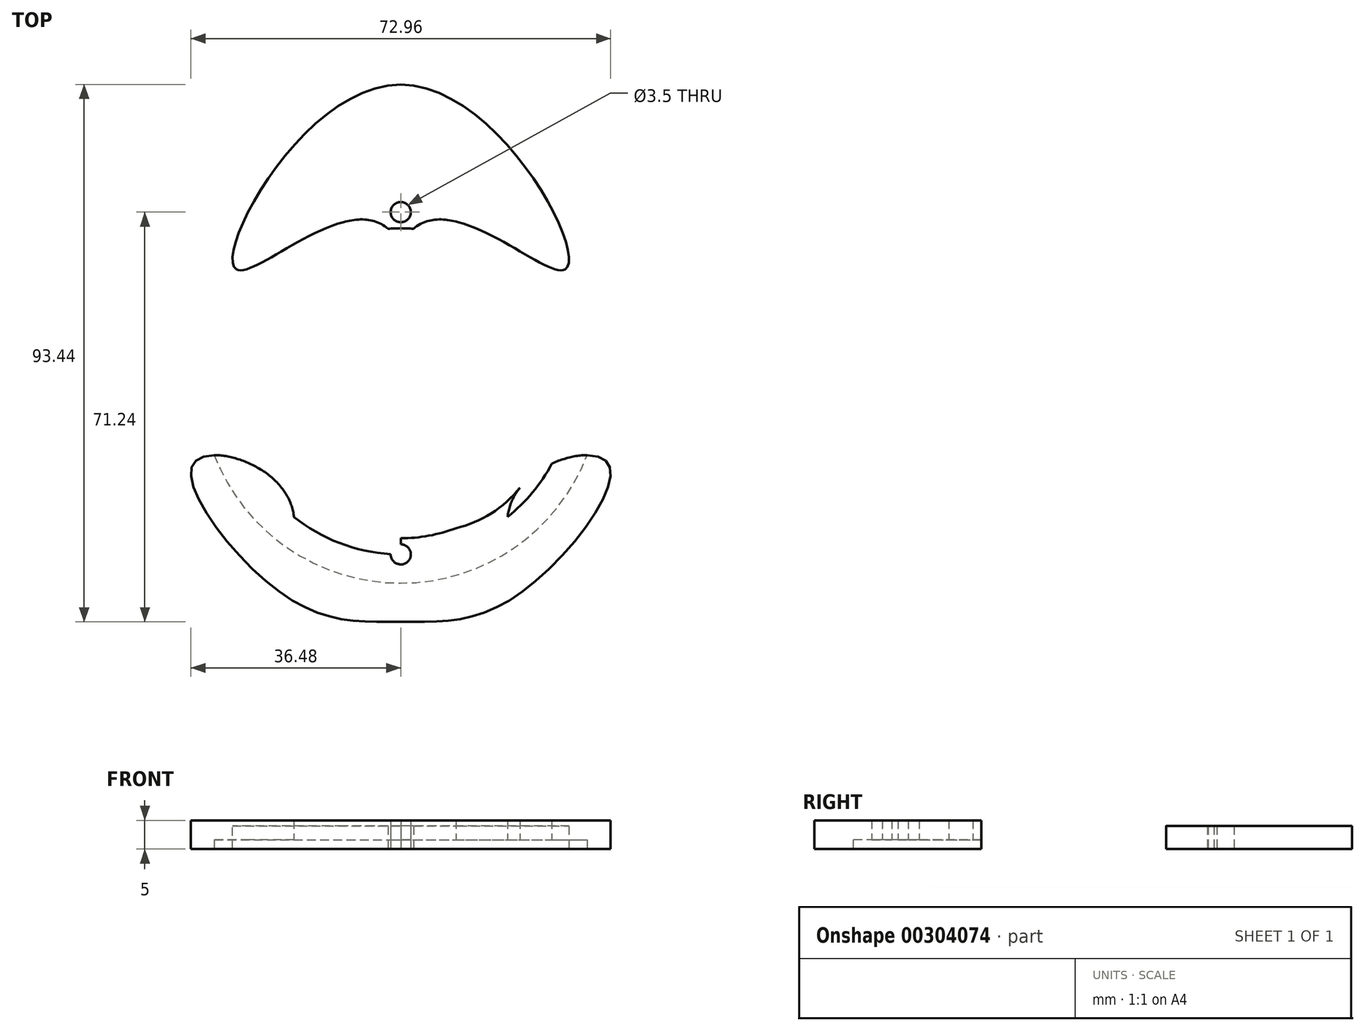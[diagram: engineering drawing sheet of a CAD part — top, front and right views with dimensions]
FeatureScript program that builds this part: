
annotation { "Feature Type Name" : "Feature", "Feature Type Description" : "" }
export const myFeature = defineFeature(function(context is Context, id is Id, definition is map)
    precondition{}
    {
        {
            var Q0;
            Q0=qCreatedBy(makeId("Top.planeOp"),FACE);
            var sketch = newSketch(context, id + "F0", { "sketchPlane" : qUnion([Q0])});
            skCircle(sketch, "E0", {"center": v(0, 0) * mm, "radius": 29.75 * mm});
            skCircle(sketch, "E1.0", {"center": v(0, 0) * mm, "radius": 34.75 * mm});
            skCircle(sketch, "E2.0", {"center": v(0, 0) * mm, "radius": 26.95 * mm});
            skCircle(sketch, "E3", {"center": v(0, 29.75) * mm, "radius": 1.75 * mm});
            skLineSegment(sketch, "E4", {"start": v(0, 39.55) * mm, "end": v(0, 26.95) * mm});
            skCircle(sketch, "E5", {"center": v(0, -29.75) * mm, "radius": 1.75 * mm});
            skLineSegment(sketch, "E6", {"start": v(0, -26.95) * mm, "end": v(1.75, -26.9) * mm});
            skLineSegment(sketch, "E7", {"start": v(1.75, -26.9) * mm, "end": v(9.3, -25.25) * mm});
            skFitSpline(sketch, "E8", {"points": [v(18.58, -23.24) * mm, v(35.7, -13.5) * mm, v(20.62, -36.6) * mm, v(0, -41.48) * mm], "startDerivative": vector(8.66, 84.64) * mm, "endDerivative": vector(-64.45, 0.22) * mm});
            skArc(sketch, "E9.filletArc", {"start": v(9.3, -25.25) * mm, "mid": v(15.63, -22.69) * mm, "end": v(20.72, -18.15) * mm});
            skLineSegment(sketch, "E10", {"start": v(0, -26.95) * mm, "end": v(0, -41.48) * mm});
            skFitSpline(sketch, "E11.MirrorCS", {"points": [v(-18.58, -23.24) * mm, v(-35.7, -13.5) * mm, v(-20.62, -36.6) * mm, v(0, -41.48) * mm], "startDerivative": vector(-8.66, 84.64) * mm, "endDerivative": vector(64.45, 0.22) * mm});
            skLineSegment(sketch, "E12.MirrorCS", {"start": v(0, -26.95) * mm, "end": v(-1.75, -26.9) * mm});
            skLineSegment(sketch, "E13.MirrorCS", {"start": v(-1.75, -26.9) * mm, "end": v(-9.3, -25.25) * mm});
            skArc(sketch, "E14.MirrorCS", {"start": v(-9.3, -25.25) * mm, "mid": v(-15.63, -22.69) * mm, "end": v(-20.72, -18.15) * mm});
            skLineSegment(sketch, "E15", {"start": v(0, 26.95) * mm, "end": v(-2.22, 26.86) * mm});
            skLineSegment(sketch, "E16", {"start": v(-2.22, 26.86) * mm, "end": v(-2.22, 26.86) * mm});
            skFitSpline(sketch, "E17", {"points": [v(-2.22, 26.86) * mm, v(-28.57, 19.79) * mm, v(0, 51.95) * mm], "startDerivative": vector(-50.1, 44.21) * mm, "endDerivative": vector(93.8, 1.88) * mm});
            skLineSegment(sketch, "E18", {"start": v(0, 51.95) * mm, "end": v(0, 39.55) * mm});
            skFitSpline(sketch, "E19.MirrorCS", {"points": [v(2.22, 26.86) * mm, v(28.57, 19.79) * mm, v(0, 51.95) * mm], "startDerivative": vector(50.1, 44.21) * mm, "endDerivative": vector(-93.8, 1.88) * mm});
            skSolve(sketch);
        }
        {
            var Q0;
            {var subQ3=sQuery(id+"F0.wireOp",EDGE,"E0");var subQ5=sQuery(id+"F0.wireOp",EDGE,"E5");var subQ6=makeQuery(id+"F0.imprint","INTERSECT",VERTEX,{"disambiguationData":[OD(1.0)],"derivedFrom":[subQ3,subQ5]});Q0=makeQuery(id+"F0.imprint","IMPRINT",FACE,{"disambiguationData":[TD([[makeQuery(id+"F0.imprint","IMPRINT",EDGE,{"disambiguationData":[TD([[subQ6,-1.0]])],"derivedFrom":subQ3}),-1.0]])]});}
            var Q1;
            {var subQ0=sQuery(id+"F0.wireOp",EDGE,"E8");var subQ1=sQuery(id+"F0.wireOp",EDGE,"E1.0");var subQ2=makeQuery(id+"F0.imprint","INTERSECT",VERTEX,{"derivedFrom":[subQ1,subQ0]});Q1=makeQuery(id+"F0.imprint","IMPRINT",FACE,{"disambiguationData":[TD([[makeQuery(id+"F0.imprint","IMPRINT",EDGE,{"disambiguationData":[TD([[subQ2,1.0]])],"derivedFrom":subQ1}),-1.0]])]});}
            var Q2;
            {var subQ7=sQuery(id+"F0.wireOp",EDGE,"E5");var subQ8=sQuery(id+"F0.wireOp",EDGE,"E0");var subQ9=makeQuery(id+"F0.imprint","INTERSECT",VERTEX,{"disambiguationData":[OD(1.0)],"derivedFrom":[subQ8,subQ7]});Q2=makeQuery(id+"F0.imprint","IMPRINT",FACE,{"disambiguationData":[TD([[makeQuery(id+"F0.imprint","IMPRINT",EDGE,{"disambiguationData":[TD([[subQ9,-1.0]])],"derivedFrom":subQ8}),1.0]])]});}
            var Q3;
            {var subQ0=sQuery(id+"F0.wireOp",EDGE,"E11.MirrorCS");var subQ1=sQuery(id+"F0.wireOp",EDGE,"E1.0");var subQ2=makeQuery(id+"F0.imprint","INTERSECT",VERTEX,{"derivedFrom":[subQ1,subQ0]});Q3=makeQuery(id+"F0.imprint","IMPRINT",FACE,{"disambiguationData":[TD([[makeQuery(id+"F0.imprint","IMPRINT",EDGE,{"disambiguationData":[TD([[subQ2,-1.0]])],"derivedFrom":subQ1}),-1.0]])]});}
            var Q4;
            {var subQ5=sQuery(id+"F0.wireOp",EDGE,"E11.MirrorCS");var subQ7=sQuery(id+"F0.wireOp",EDGE,"E0");var subQ9=makeQuery(id+"F0.imprint","INTERSECT",VERTEX,{"derivedFrom":[subQ7,subQ5]});Q4=makeQuery(id+"F0.imprint","IMPRINT",FACE,{"disambiguationData":[TD([[makeQuery(id+"F0.imprint","IMPRINT",EDGE,{"disambiguationData":[TD([[subQ9,-1.0]])],"derivedFrom":subQ7}),-1.0]])]});}
            var Q5;
            {var subQ1=sQuery(id+"F0.wireOp",EDGE,"E0");var subQ11=sQuery(id+"F0.wireOp",EDGE,"E11.MirrorCS");var subQ12=makeQuery(id+"F0.imprint","INTERSECT",VERTEX,{"derivedFrom":[subQ1,subQ11]});Q5=makeQuery(id+"F0.imprint","IMPRINT",FACE,{"disambiguationData":[TD([[makeQuery(id+"F0.imprint","IMPRINT",EDGE,{"disambiguationData":[TD([[subQ12,-1.0]])],"derivedFrom":subQ1}),1.0]])]});}
            extrude(context, id + "F1", {"entities" : qUnion([Q0, Q1, Q2, Q3, Q4, Q5]), "depth" : 5 * mm});
        }
        {
            var Q0;
            {var subQ0=sQuery(id+"F0.wireOp",EDGE,"0fa87bf3-afe1-459e-863f-c668f79fc1950.MirrorCS");var subQ1=sQuery(id+"F0.wireOp",EDGE,"E0");var subQ2=makeQuery(id+"F0.imprint","INTERSECT",VERTEX,{"derivedFrom":[subQ1,subQ0]});Q0=makeQuery(id+"F0.imprint","IMPRINT",FACE,{"disambiguationData":[TD([[makeQuery(id+"F0.imprint","IMPRINT",EDGE,{"disambiguationData":[TD([[subQ2,-1.0]])],"derivedFrom":subQ1}),-1.0]])]});}
            var Q1;
            {var subQ5=sQuery(id+"F0.wireOp",EDGE,"E11.MirrorCS");var subQ7=sQuery(id+"F0.wireOp",EDGE,"E0");var subQ9=makeQuery(id+"F0.imprint","INTERSECT",VERTEX,{"derivedFrom":[subQ7,subQ5]});Q1=makeQuery(id+"F0.imprint","IMPRINT",FACE,{"disambiguationData":[TD([[makeQuery(id+"F0.imprint","IMPRINT",EDGE,{"disambiguationData":[TD([[subQ9,-1.0]])],"derivedFrom":subQ7}),-1.0]])]});}
            var Q2;
            {var subQ3=sQuery(id+"F0.wireOp",EDGE,"E0");var subQ5=sQuery(id+"F0.wireOp",EDGE,"E5");var subQ6=makeQuery(id+"F0.imprint","INTERSECT",VERTEX,{"disambiguationData":[OD(1.0)],"derivedFrom":[subQ3,subQ5]});Q2=makeQuery(id+"F0.imprint","IMPRINT",FACE,{"disambiguationData":[TD([[makeQuery(id+"F0.imprint","IMPRINT",EDGE,{"disambiguationData":[TD([[subQ6,-1.0]])],"derivedFrom":subQ3}),-1.0]])]});}
            var Q3;
            {var subQ0=sQuery(id+"F0.wireOp",EDGE,"E10");var subQ1=sQuery(id+"F0.wireOp",EDGE,"E0");var subQ2=makeQuery(id+"F0.imprint","INTERSECT",VERTEX,{"derivedFrom":[subQ1,subQ0]});Q3=makeQuery(id+"F0.imprint","IMPRINT",FACE,{"disambiguationData":[TD([[makeQuery(id+"F0.imprint","IMPRINT",EDGE,{"disambiguationData":[TD([[subQ2,-1.0]])],"derivedFrom":subQ1}),-1.0]])]});}
            var Q4;
            {var subQ0=sQuery(id+"F0.wireOp",EDGE,"E5");var subQ1=sQuery(id+"F0.wireOp",EDGE,"E0");var subQ2=makeQuery(id+"F0.imprint","INTERSECT",VERTEX,{"disambiguationData":[OD(0.0)],"derivedFrom":[subQ1,subQ0]});Q4=makeQuery(id+"F0.imprint","IMPRINT",FACE,{"disambiguationData":[TD([[makeQuery(id+"F0.imprint","IMPRINT",EDGE,{"disambiguationData":[TD([[subQ2,-1.0]])],"derivedFrom":subQ1}),-1.0]])]});}
            var Q5;
            {var subQ0=sQuery(id+"F0.wireOp",EDGE,"rNSyIOqq-r5HT-ujXF-LOEd-3bkf5kpP6Zm5");var subQ1=sQuery(id+"F0.wireOp",EDGE,"E0");var subQ2=makeQuery(id+"F0.imprint","INTERSECT",VERTEX,{"derivedFrom":[subQ1,subQ0]});Q5=makeQuery(id+"F0.imprint","IMPRINT",FACE,{"disambiguationData":[TD([[makeQuery(id+"F0.imprint","IMPRINT",EDGE,{"disambiguationData":[TD([[subQ2,1.0]])],"derivedFrom":subQ1}),-1.0]])]});}
            var Q6;
            {var subQ0=sQuery(id+"F0.wireOp",EDGE,"rNSyIOqq-r5HT-ujXF-LOEd-3bkf5kpP6Zm5");var subQ7=sQuery(id+"F0.wireOp",EDGE,"E0");var subQ9=makeQuery(id+"F0.imprint","INTERSECT",VERTEX,{"derivedFrom":[subQ7,subQ0]});Q6=makeQuery(id+"F0.imprint","IMPRINT",FACE,{"disambiguationData":[TD([[makeQuery(id+"F0.imprint","IMPRINT",EDGE,{"disambiguationData":[TD([[subQ9,1.0]])],"derivedFrom":subQ7}),1.0]])]});}
            var Q7;
            {var subQ7=sQuery(id+"F0.wireOp",EDGE,"E5");var subQ8=sQuery(id+"F0.wireOp",EDGE,"E0");var subQ9=makeQuery(id+"F0.imprint","INTERSECT",VERTEX,{"disambiguationData":[OD(1.0)],"derivedFrom":[subQ8,subQ7]});Q7=makeQuery(id+"F0.imprint","IMPRINT",FACE,{"disambiguationData":[TD([[makeQuery(id+"F0.imprint","IMPRINT",EDGE,{"disambiguationData":[TD([[subQ9,-1.0]])],"derivedFrom":subQ8}),1.0]])]});}
            var Q8;
            {var subQ1=sQuery(id+"F0.wireOp",EDGE,"E0");var subQ11=sQuery(id+"F0.wireOp",EDGE,"E11.MirrorCS");var subQ12=makeQuery(id+"F0.imprint","INTERSECT",VERTEX,{"derivedFrom":[subQ1,subQ11]});Q8=makeQuery(id+"F0.imprint","IMPRINT",FACE,{"disambiguationData":[TD([[makeQuery(id+"F0.imprint","IMPRINT",EDGE,{"disambiguationData":[TD([[subQ12,-1.0]])],"derivedFrom":subQ1}),1.0]])]});}
            var Q9;
            {var subQ0=sQuery(id+"F0.wireOp",EDGE,"E5");var subQ1=sQuery(id+"F0.wireOp",EDGE,"E0");var subQ2=makeQuery(id+"F0.imprint","INTERSECT",VERTEX,{"disambiguationData":[OD(0.0)],"derivedFrom":[subQ1,subQ0]});Q9=makeQuery(id+"F0.imprint","IMPRINT",FACE,{"disambiguationData":[TD([[makeQuery(id+"F0.imprint","IMPRINT",EDGE,{"disambiguationData":[TD([[subQ2,-1.0]])],"derivedFrom":subQ1}),1.0]])]});}
            var Q10;
            {var subQ0=sQuery(id+"F0.wireOp",EDGE,"E10");var subQ1=sQuery(id+"F0.wireOp",EDGE,"E0");var subQ2=makeQuery(id+"F0.imprint","INTERSECT",VERTEX,{"derivedFrom":[subQ1,subQ0]});Q10=makeQuery(id+"F0.imprint","IMPRINT",FACE,{"disambiguationData":[TD([[makeQuery(id+"F0.imprint","IMPRINT",EDGE,{"disambiguationData":[TD([[subQ2,-1.0]])],"derivedFrom":subQ1}),1.0]])]});}
            var Q11;
            {var subQ0=sQuery(id+"F0.wireOp",EDGE,"0fa87bf3-afe1-459e-863f-c668f79fc1950.MirrorCS");var subQ7=sQuery(id+"F0.wireOp",EDGE,"E0");var subQ9=makeQuery(id+"F0.imprint","INTERSECT",VERTEX,{"derivedFrom":[subQ7,subQ0]});Q11=makeQuery(id+"F0.imprint","IMPRINT",FACE,{"disambiguationData":[TD([[makeQuery(id+"F0.imprint","IMPRINT",EDGE,{"disambiguationData":[TD([[subQ9,-1.0]])],"derivedFrom":subQ7}),1.0]])]});}
            extrude(context, id + "F2", {"entities" : qUnion([Q0, Q1, Q2, Q3, Q4, Q5, Q6, Q7, Q8, Q9, Q10, Q11]), "operationType" : NewBodyOperationType.REMOVE, "depth" : 1.6 * mm});
        }
        {
            var Q0;
            {var subQ4=sQuery(id+"F0.wireOp",EDGE,"E0");var subQ8=sQuery(id+"F0.wireOp",EDGE,"E3");var subQ10=makeQuery(id+"F0.imprint","INTERSECT",VERTEX,{"disambiguationData":[OD(1.0)],"derivedFrom":[subQ4,subQ8]});Q0=makeQuery(id+"F0.imprint","IMPRINT",FACE,{"disambiguationData":[TD([[makeQuery(id+"F0.imprint","IMPRINT",EDGE,{"disambiguationData":[TD([[subQ10,-1.0]])],"derivedFrom":subQ4}),1.0]])]});}
            var Q1;
            {var subQ3=sQuery(id+"F0.wireOp",EDGE,"E3");var subQ7=sQuery(id+"F0.wireOp",EDGE,"E0");var subQ9=makeQuery(id+"F0.imprint","INTERSECT",VERTEX,{"disambiguationData":[OD(0.0)],"derivedFrom":[subQ7,subQ3]});Q1=makeQuery(id+"F0.imprint","IMPRINT",FACE,{"disambiguationData":[TD([[makeQuery(id+"F0.imprint","IMPRINT",EDGE,{"disambiguationData":[TD([[subQ9,1.0]])],"derivedFrom":subQ7}),1.0]])]});}
            var Q2;
            {var subQ3=sQuery(id+"F0.wireOp",EDGE,"E3");var subQ7=sQuery(id+"F0.wireOp",EDGE,"E0");var subQ9=makeQuery(id+"F0.imprint","INTERSECT",VERTEX,{"disambiguationData":[OD(0.0)],"derivedFrom":[subQ7,subQ3]});Q2=makeQuery(id+"F0.imprint","IMPRINT",FACE,{"disambiguationData":[TD([[makeQuery(id+"F0.imprint","IMPRINT",EDGE,{"disambiguationData":[TD([[subQ9,1.0]])],"derivedFrom":subQ7}),-1.0]])]});}
            var Q3;
            {var subQ5=sQuery(id+"F0.wireOp",EDGE,"E18");Q3=makeQuery(id+"F0.imprint","IMPRINT",FACE,{"disambiguationData":[TD([[makeQuery(id+"F0.imprint","IMPRINT",EDGE,{"derivedFrom":subQ5}),1.0]])]});}
            var Q4;
            {var subQ5=sQuery(id+"F0.wireOp",EDGE,"E18");Q4=makeQuery(id+"F0.imprint","IMPRINT",FACE,{"disambiguationData":[TD([[makeQuery(id+"F0.imprint","IMPRINT",EDGE,{"derivedFrom":subQ5}),-1.0]])]});}
            var Q5;
            {var subQ3=sQuery(id+"F0.wireOp",EDGE,"E3");var subQ5=sQuery(id+"F0.wireOp",EDGE,"E0");var subQ6=makeQuery(id+"F0.imprint","INTERSECT",VERTEX,{"disambiguationData":[OD(1.0)],"derivedFrom":[subQ5,subQ3]});Q5=makeQuery(id+"F0.imprint","IMPRINT",FACE,{"disambiguationData":[TD([[makeQuery(id+"F0.imprint","IMPRINT",EDGE,{"disambiguationData":[TD([[subQ6,-1.0]])],"derivedFrom":subQ5}),-1.0]])]});}
            extrude(context, id + "F3", {"entities" : qUnion([Q0, Q1, Q2, Q3, Q4, Q5]), "depth" : 4 * mm});
        }
    });
